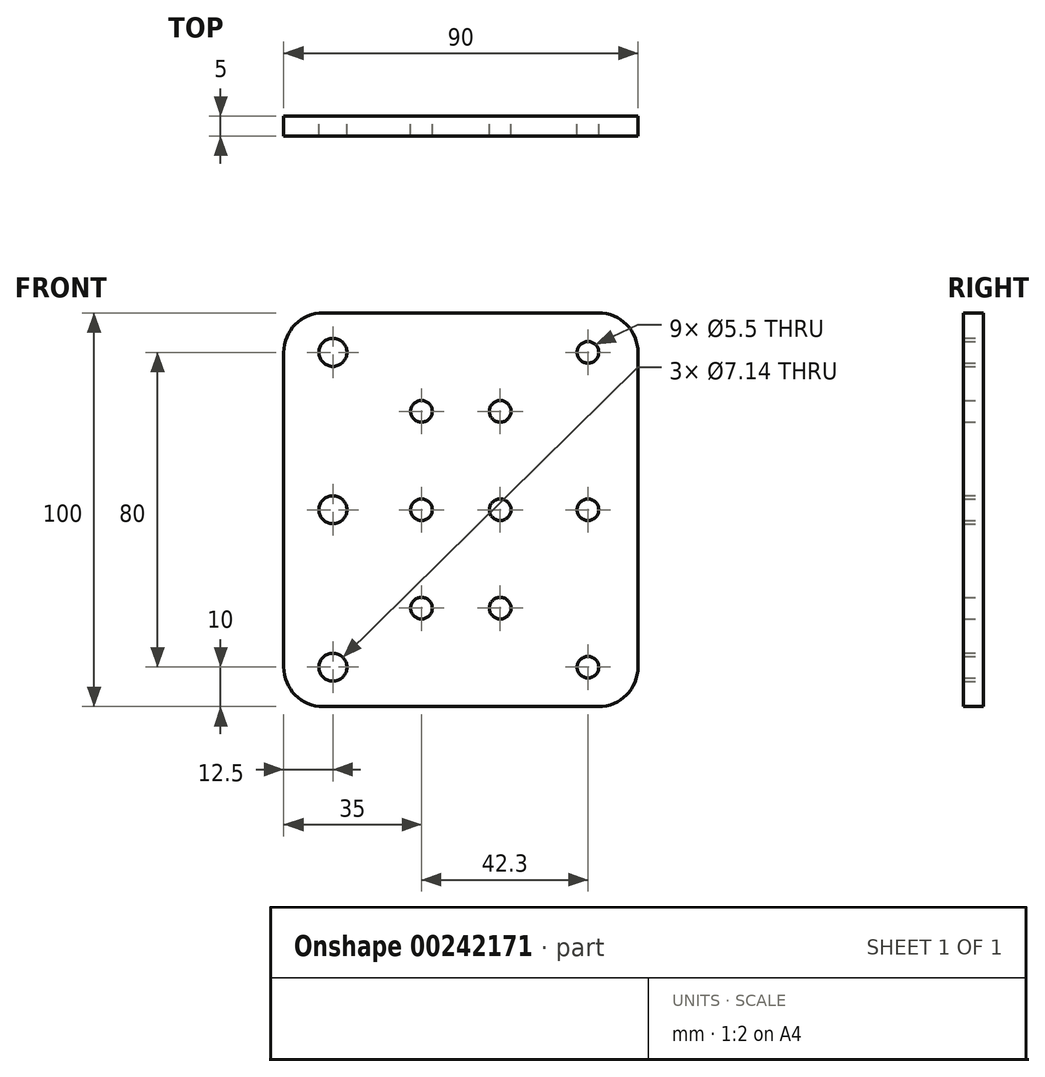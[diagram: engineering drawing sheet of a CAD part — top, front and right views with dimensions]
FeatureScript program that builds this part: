
annotation { "Feature Type Name" : "Feature", "Feature Type Description" : "" }
export const myFeature = defineFeature(function(context is Context, id is Id, definition is map)
    precondition{}
    {
        {
            var Q0;
            Q0=qCreatedBy(makeId("Front.planeOp"),FACE);
            var sketch = newSketch(context, id + "F0", { "sketchPlane" : qUnion([Q0])});
            skLineSegment(sketch, "E0.bottom", {"start": v(35, -50) * mm, "end": v(-35, -50) * mm});
            skLineSegment(sketch, "E0.top", {"start": v(35, 50) * mm, "end": v(-35, 50) * mm});
            skLineSegment(sketch, "E0.left", {"start": v(45, -40) * mm, "end": v(45, 40) * mm});
            skLineSegment(sketch, "E0.right", {"start": v(-45, -40) * mm, "end": v(-45, 40) * mm});
            skPoint(sketch, "E0.middle", {"position": v(0, 0) * mm});
            skPoint(sketch, "E1.visualSharp", {"position": v(-45, 50) * mm});
            skArc(sketch, "E1.filletArc", {"start": v(-35, 50) * mm, "mid": v(-42.07, 47.07) * mm, "end": v(-45, 40) * mm});
            skPoint(sketch, "E2.visualSharp", {"position": v(45, 50) * mm});
            skArc(sketch, "E2.filletArc", {"start": v(45, 40) * mm, "mid": v(42.07, 47.07) * mm, "end": v(35, 50) * mm});
            skPoint(sketch, "E3.visualSharp", {"position": v(45, -50) * mm});
            skArc(sketch, "E3.filletArc", {"start": v(35, -50) * mm, "mid": v(42.07, -47.07) * mm, "end": v(45, -40) * mm});
            skPoint(sketch, "E4.visualSharp", {"position": v(-45, -50) * mm});
            skArc(sketch, "E4.filletArc", {"start": v(-45, -40) * mm, "mid": v(-42.07, -47.07) * mm, "end": v(-35, -50) * mm});
            skLineSegment(sketch, "E5", {"start": v(-32.5, 50) * mm, "end": v(-32.5, -50) * mm, "construction": true});
            skLineSegment(sketch, "E6", {"start": v(-45, -40) * mm, "end": v(45, -40) * mm, "construction": true});
            skLineSegment(sketch, "E7", {"start": v(-45, 40) * mm, "end": v(45, 40) * mm, "construction": true});
            skCircle(sketch, "E8", {"center": v(-32.5, -40) * mm, "radius": 3.57 * mm});
            skCircle(sketch, "E9", {"center": v(-32.5, 0) * mm, "radius": 3.57 * mm});
            skCircle(sketch, "E10", {"center": v(-32.5, 40) * mm, "radius": 3.57 * mm});
            skLineSegment(sketch, "E11", {"start": v(-45, -25) * mm, "end": v(45, -25) * mm, "construction": true});
            skLineSegment(sketch, "E12", {"start": v(-10, 50) * mm, "end": v(-10, -50) * mm, "construction": true});
            skCircle(sketch, "E13", {"center": v(-10, -25) * mm, "radius": 2.75 * mm});
            skCircle(sketch, "E14", {"center": v(-10, 0) * mm, "radius": 2.75 * mm});
            skLineSegment(sketch, "E15", {"start": v(45, 0) * mm, "end": v(-45, 0) * mm, "construction": true});
            skCircle(sketch, "E16.MirrorC", {"center": v(-10, 25) * mm, "radius": 2.75 * mm});
            skLineSegment(sketch, "E17", {"start": v(45, 25) * mm, "end": v(-45, 25) * mm, "construction": true});
            skLineSegment(sketch, "E18", {"start": v(0, 50) * mm, "end": v(0, -50) * mm, "construction": true});
            skCircle(sketch, "E19.MirrorC", {"center": v(10, 25) * mm, "radius": 2.75 * mm});
            skCircle(sketch, "E20.MirrorC", {"center": v(10, 0) * mm, "radius": 2.75 * mm});
            skLineSegment(sketch, "E21", {"start": v(10, 50) * mm, "end": v(10, -50) * mm, "construction": true});
            skCircle(sketch, "E22.MirrorC", {"center": v(10, -25) * mm, "radius": 2.75 * mm});
            skLineSegment(sketch, "E23", {"start": v(32.3, 50) * mm, "end": v(32.3, -50) * mm, "construction": true});
            skCircle(sketch, "E24", {"center": v(32.3, 40) * mm, "radius": 2.75 * mm});
            skCircle(sketch, "E25", {"center": v(32.3, 0) * mm, "radius": 2.75 * mm});
            skCircle(sketch, "E26", {"center": v(32.3, -40) * mm, "radius": 2.75 * mm});
            skSolve(sketch);
        }
        {
            var Q0;
            Q0=makeQuery(id+"F0.imprint","IMPRINT",FACE,{"disambiguationData":[TD([[makeQuery(id+"F0.imprint","IMPRINT",EDGE,{"derivedFrom":sQuery(id+"F0.wireOp",EDGE,"E0.bottom")}),-1.0]])]});
            extrude(context, id + "F1", {"entities" : qUnion([Q0]), "depth" : 5 * mm});
        }
    });
